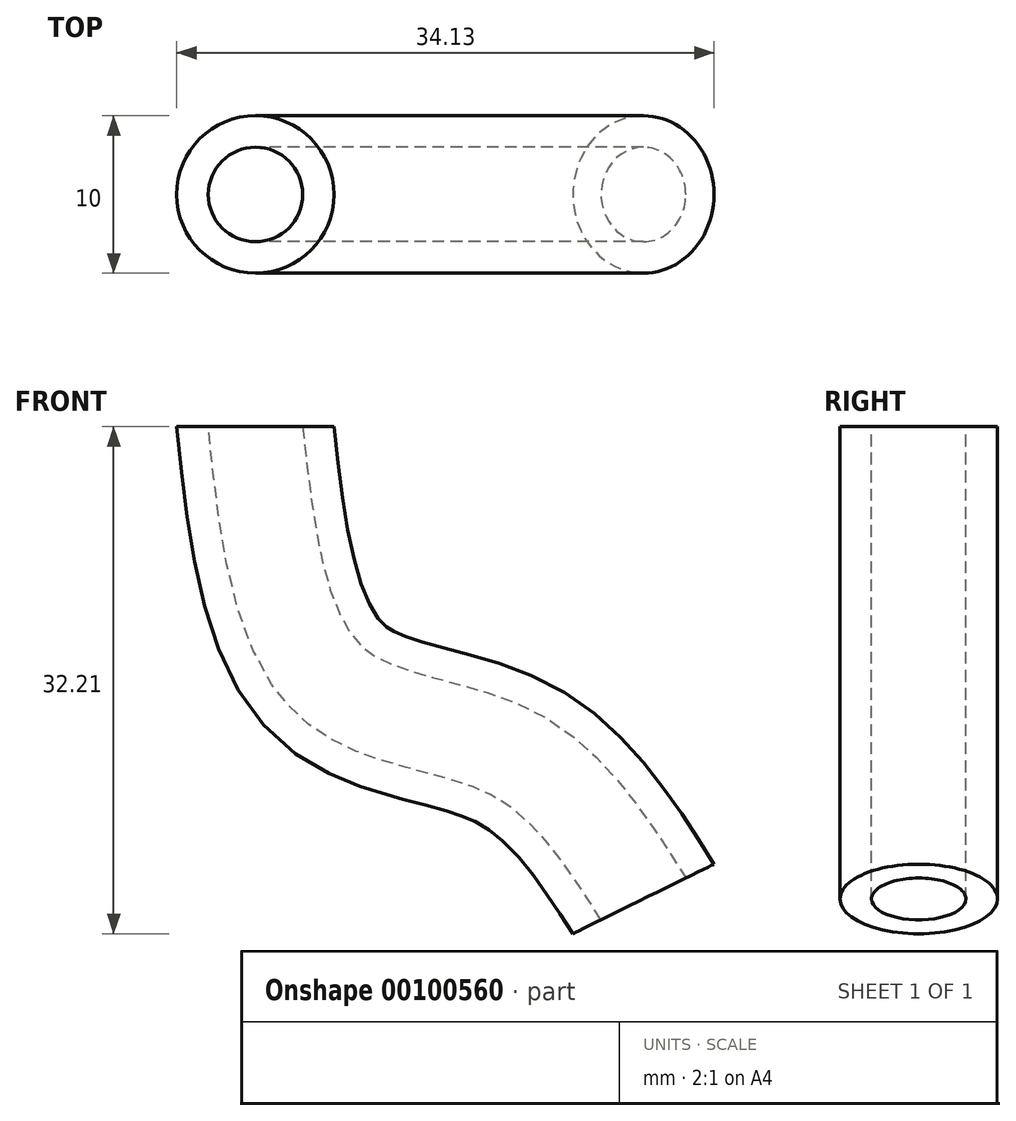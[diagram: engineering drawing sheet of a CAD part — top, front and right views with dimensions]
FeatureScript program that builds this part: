
annotation { "Feature Type Name" : "Feature", "Feature Type Description" : "" }
export const myFeature = defineFeature(function(context is Context, id is Id, definition is map)
    precondition{}
    {
        {
            var Q0;
            Q0=qCreatedBy(makeId("Top.planeOp"),FACE);
            var sketch = newSketch(context, id + "F0", { "sketchPlane" : qUnion([Q0])});
            skCircle(sketch, "E0", {"center": v(0, 0) * mm, "radius": 5 * mm});
            skCircle(sketch, "E1", {"center": v(0, 0) * mm, "radius": 3 * mm});
            skSolve(sketch);
        }
        {
            var Q0;
            Q0=qCreatedBy(makeId("Front.planeOp"),FACE);
            var sketch = newSketch(context, id + "F1", { "sketchPlane" : qUnion([Q0])});
            skFitSpline(sketch, "E2", {"points": [v(0, 0) * mm, v(4.85, -16.25) * mm, v(16.27, -20.7) * mm, v(24.64, -30) * mm], "startDerivative": vector(5.75, -53.64) * mm, "endDerivative": vector(22.31, -35.18) * mm});
            skSolve(sketch);
        }
        {
            var Q0;
            Q0=makeQuery(id+"F0.imprint","IMPRINT",FACE,{"disambiguationData":[TD([[makeQuery(id+"F0.imprint","IMPRINT",EDGE,{"derivedFrom":sQuery(id+"F0.wireOp",EDGE,"E0")}),1.0]])]});
            var Q1;
            Q1=sQuery(id+"F1.wireOp",EDGE,"E2");
            sweep(context, id + "F2", {"profiles" : qUnion([Q0]), "path" : qUnion([Q1])});
        }
    });
